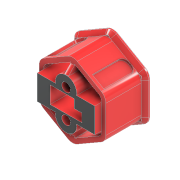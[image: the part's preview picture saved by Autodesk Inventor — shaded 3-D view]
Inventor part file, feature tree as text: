
AUTODESK INVENTOR PART (.ipt)
format: ipt  version: 2021 (Build 250183000, 183)  size: 950,784 bytes
history: native  units: mm
features: extrude x11, delete_face x9, sketch x8, projected_geometry x8, reference x6, chamfer x5, other x5, hole x1, plane x1
ambient origin geometry x8: Origin, YZ Plane, XZ Plane, XY Plane, X Axis, Y Axis, Z Axis, Center Point
bodies: Volumenkörper1 (feature_tree), Body1 (feature_tree)
feature tree (54):
  delete_face  "Fläche löschen1"
  extrude  "Extrusion1"  TaperAngle=30.0deg  [1 undecoded]
  delete_face  "Fläche löschen2"
  delete_face  "Fläche löschen3"
  delete_face  "Fläche löschen4"
  extrude  "Extrusion2"  Depth=0.1mm TaperAngle=0.0deg
  extrude  "Extrusion3"  Depth=2.75mm
  chamfer  "Fase1"  Distance=2.75mm
  extrude  "Extrusion4"  TaperAngle=0.0deg  [1 undecoded]
  chamfer  "Fase2"  Distance=0.4mm
  other  "Prägen1"
  delete_face  "Fläche löschen5"
  delete_face  "Fläche löschen6"
  sketch  "Skizze6"  dims[d12=0.0mm]
  extrude  "Extrusion5"  Depth=0.4mm
  delete_face  "Fläche löschen7"
  extrude  "Extrusion6"  Depth=2.5mm
  hole  "Bohrung1"  [1 undecoded]
  plane  "Arbeitsebene1"
  extrude  "Extrusion7"  Depth=0.4mm
  chamfer  "Fase4"  Distance=0.4mm
  extrude  "Extrusion8"  Depth=1.4mm TaperAngle=0.0deg
  delete_face  "Fläche löschen8"
  chamfer  "Fase5"  Distance=2.0mm Angle=45.0deg
  chamfer  "Fase6"  Distance=1.0mm
  extrude  "Extrusion9"  Depth=2.0mm TaperAngle=45.0deg
  extrude  "Extrusion10"  Depth=2.0mm
  delete_face  "Fläche löschen9"
  extrude  "Extrusion11"  Depth=2.0mm
  sketch  "Skizze1"  dims[d2=0.2mm d3=30.0deg]
  projected_geometry  "Projizierte Kontur1"
  projected_geometry  "Projizierte Kontur2"
  sketch  "Skizze2"  dims[d4=0.2mm d5=0.1mm d6=0.0mm]
  reference  "Referenz1"
  reference  "Referenz2"
  reference  "Referenz3"
  reference  "Referenz4"
  reference  "Referenz5"
  reference  "Referenz6"
  sketch  "Skizze3"  dims[d7=10.3mm d8=2.75mm]
  projected_geometry  "Projizierte Kontur3"
  sketch  "Skizze4"  dims[d10=0.05mm]
  projected_geometry  "Projizierte Kontur4"
  sketch  "Skizze5"  dims[d11=10.2mm]
  projected_geometry  "Projizierte Kontur5"
  sketch  "Skizze7"  dims[d13=7.8mm]
  other  "Bild1"
  projected_geometry  "Projizierte Kontur6"
  projected_geometry  "Projizierte Kontur7"
  sketch  "Skizze9"  dims[d14=7.7mm d15=2.75mm d16=0.0mm d17=0.0mm d18=0.4mm d19=0.4mm d20=2.5mm d21=0.4mm d22=0.4mm d23=0.4mm d24=1.4mm d25=0.0mm d26=1.2mm d27=2.0mm d28=45.0deg d29=1.0mm d30=0.0mm d31=0.2mm d32=2.0mm d33=45.0deg d34=2.0mm d35=2.0mm d36=0.65mm d37=0.0mm d42=5.56mm d43=4.375mm d44=4.6mm d45=6.9mm d46=180.0deg d47=0.0mm d48=0.0mm d49=0.0mm d50=1.0mm d51=0.0mm d52=2.84mm d53=6.0mm d54=4.0mm d55=2.0mm d56=90.0deg d57=13.0mm d58=0.0mm d59=1.0mm d60=0.0mm d61=2.0mm d62=2.0mm d63=45.0deg d107=6.0mm d108=6.0mm d111=3.9mm d112=21.554816mm d113=3.9mm d114=21.554816mm d115=7.8mm d116=9.86111mm d117=1.55mm d118=1.55mm d119=1.55mm d120=180.0deg d121=21.554816mm d122=1.55mm d123=3.9mm d124=21.554816mm d127=1.55mm d128=0.0mm d129=1.35mm d130=1.35mm d131=7.35mm d132=8.325mm d133=8.325mm d134=1.0mm d135=0.0mm d136=0.64626mm d137=2.0mm d138=45.0deg d139=0.353mm d140=2.0mm d141=45.0deg d142=3.7mm d143=0.0mm d144=4.6mm d145=5.56mm d147=6.9mm d149=1.0mm d150=0.0mm d151=1.0mm d152=0.0mm d153=1.5mm d154=0.0mm]
  projected_geometry  "Projizierte Kontur9"
  other  "<userpath>\Desktop\Voron-2-2.4r1\Custom\Adxl Connector\Adxl Connector.iam"
  other  "Adxl Connector.iam"
  other  "Plug 3+4Pin:1"
note: 3 required parameter values undecoded (feature->parameter linkage not recoverable at this tier; creation-order binding heuristic only, values carry confidence <= 0.55)
